# Revit family: Zumtobel VIVO II M - Recessed
name_source: partatom
category: Lighting Fixtures
revit_build: Autodesk Revit 2016 (Build: 20150220_1215(x64)
units: mm (PartAtom-declared; Revit-internal decimal feet)

## family parameters
Cut with Voids When Loaded = No
Host = Face
Light Source = No
OmniClass Number = 23.80.70.11
OmniClass Title = Luminaries for Internal Lighting
Part Type = Normal
Room Calculation Point = No
Round Connector Dimension = Use Diameter
Shared = No

## types (1)
- VIV2-R M 2800-930 SWI FL WH WH
    Apparent Load = 30 VA
    Assembly Code = D5020200
    Default Elevation = 0 mm  [stored 0 ft]
    Description = Recessed swivelling spotlight
    Emit Shape Visible in Rendering = No
    Height = 66 mm  [stored 0.216535 ft]
    Lamp = LED
    Length = 95 mm
    Manufacturer = Zumtobel Lighting
    Model = 60715752
    URL = http://www.zumtobel.com
    Voltage = 230 V
    Width = 95 mm

note: [stored X ft] marks values corroborated as IEEE doubles in the binary element streams (Revit-internal decimal feet)

## geometry (parser evidence)
native form markers: Sweep x6
no freeform markers — native parametric forms only
